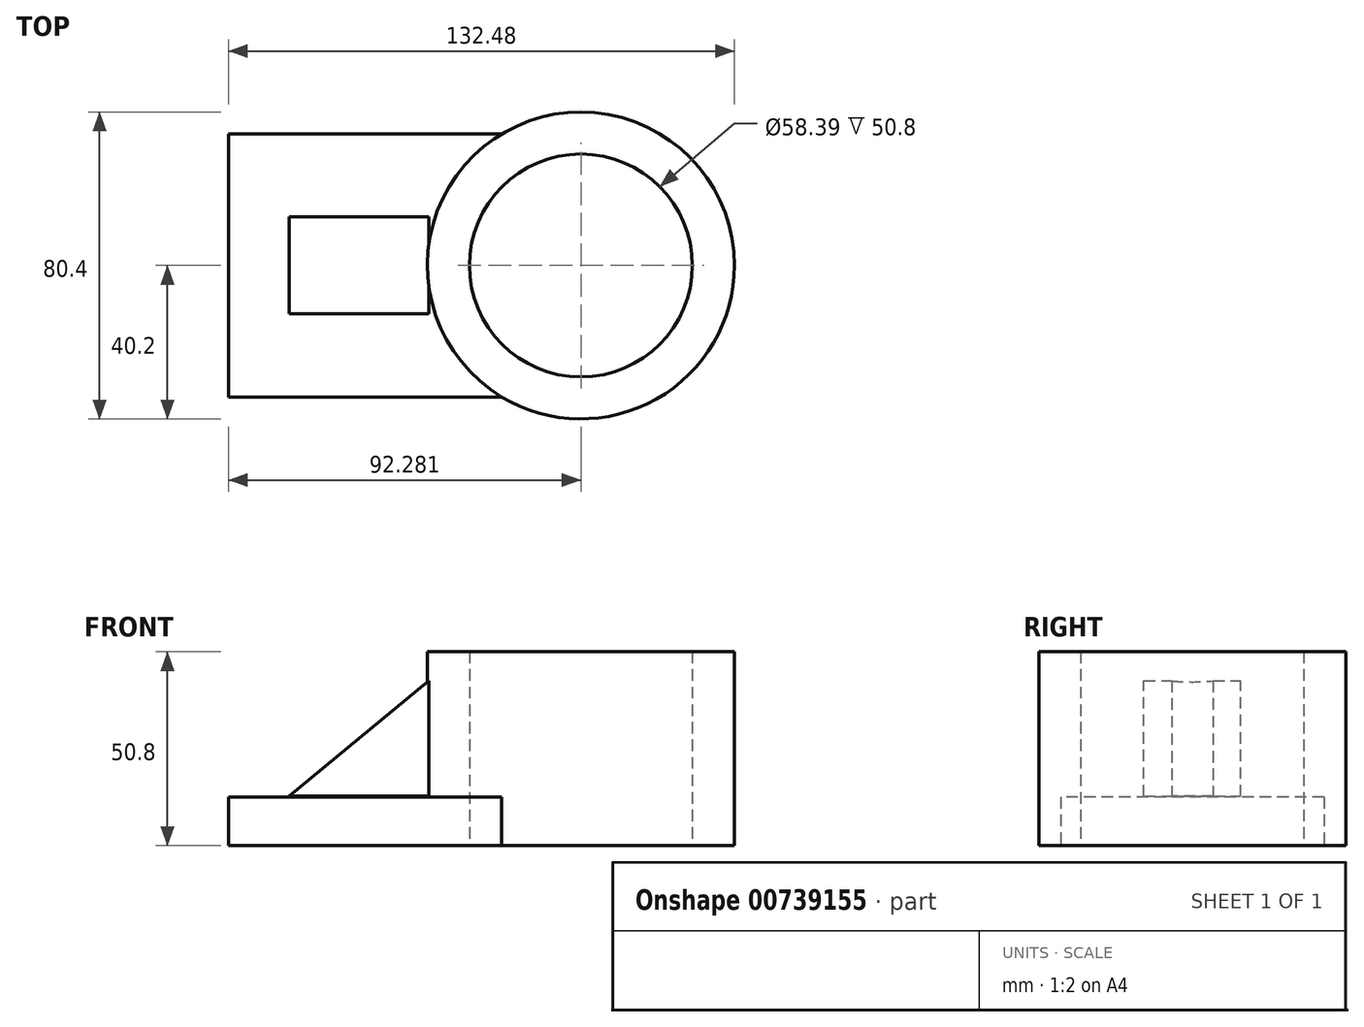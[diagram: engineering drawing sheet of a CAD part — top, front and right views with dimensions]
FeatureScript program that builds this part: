
annotation { "Feature Type Name" : "Feature", "Feature Type Description" : "" }
export const myFeature = defineFeature(function(context is Context, id is Id, definition is map)
    precondition{}
    {
        {
            var Q0;
            Q0=qCreatedBy(makeId("Top.planeOp"),FACE);
            var sketch = newSketch(context, id + "F0", { "sketchPlane" : qUnion([Q0])});
            skLineSegment(sketch, "E0.bottom", {"start": v(-46.14, 34.44) * mm, "end": v(25.4, 34.44) * mm});
            skLineSegment(sketch, "E0.top", {"start": v(-46.14, -34.44) * mm, "end": v(25.4, -34.44) * mm});
            skLineSegment(sketch, "E0.left", {"start": v(-46.14, 34.44) * mm, "end": v(-46.14, -34.44) * mm});
            skPoint(sketch, "E0.middle", {"position": v(0, 0) * mm});
            skCircle(sketch, "E1", {"center": v(46.14, 0) * mm, "radius": 40.2 * mm});
            skPoint(sketch, "E2.orphan", {"position": v(46.14, 34.44) * mm});
            skPoint(sketch, "E3.orphan", {"position": v(46.14, -34.44) * mm});
            skCircle(sketch, "E4", {"center": v(46.14, 0) * mm, "radius": 29.2 * mm});
            skSolve(sketch);
        }
        {
            var Q0;
            {var subQ0=sQuery(id+"F0.wireOp",EDGE,"E0.left");Q0=makeQuery(id+"F0.imprint","IMPRINT",FACE,{"disambiguationData":[TD([[makeQuery(id+"F0.imprint","IMPRINT",EDGE,{"derivedFrom":subQ0}),1.0]])]});}
            extrude(context, id + "F1", {"entities" : qUnion([Q0]), "depth" : 12.7 * mm, "offsetDistance" : 25.4 * mm});
        }
        {
            var Q0;
            {var subQ0=sQuery(id+"F0.wireOp",EDGE,"E1");var subQ1=makeQuery(id+"F0.imprint","INTERSECT",VERTEX,{"derivedFrom":[sQuery(id+"F0.wireOp",EDGE,"E0.bottom"),subQ0]});Q0=makeQuery(id+"F0.imprint","IMPRINT",FACE,{"disambiguationData":[TD([[makeQuery(id+"F0.imprint","IMPRINT",EDGE,{"disambiguationData":[TD([[subQ1,-1.0]])],"derivedFrom":subQ0}),1.0]])]});}
            extrude(context, id + "F2", {"entities" : qUnion([Q0]), "operationType" : NewBodyOperationType.ADD, "depth" : 50.8 * mm, "offsetDistance" : 25.4 * mm});
        }
        {
            var Q0;
            Q0=qCreatedBy(makeId("Front.planeOp"),FACE);
            var sketch = newSketch(context, id + "F3", { "sketchPlane" : qUnion([Q0])});
            skLineSegment(sketch, "E5", {"start": v(6.3, 43.2) * mm, "end": v(-30.22, 12.94) * mm});
            skLineSegment(sketch, "E6", {"start": v(-30.22, 12.94) * mm, "end": v(6.3, 12.94) * mm});
            skLineSegment(sketch, "E7", {"start": v(6.3, 12.94) * mm, "end": v(6.3, 43.2) * mm});
            skSolve(sketch);
        }
        {
            var Q0;
            Q0 = qSketchRegion(id + "F3", true);
            extrude(context, id + "F4", {"entities" : qUnion([Q0]), "operationType" : NewBodyOperationType.ADD, "endBound" : BoundingType.SYMMETRIC, "depth" : 25.4 * mm, "offsetDistance" : 25.4 * mm});
        }
    });
